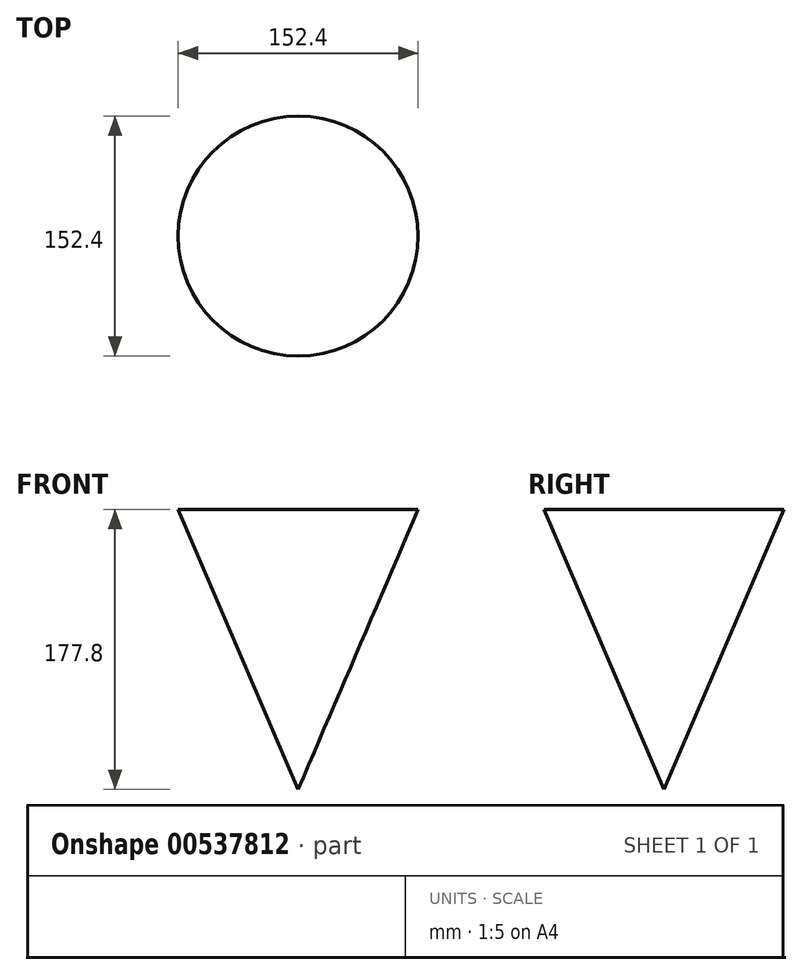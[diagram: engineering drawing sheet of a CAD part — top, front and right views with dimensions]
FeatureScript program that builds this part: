
annotation { "Feature Type Name" : "Feature", "Feature Type Description" : "" }
export const myFeature = defineFeature(function(context is Context, id is Id, definition is map)
    precondition{}
    {
        {
            var Q0;
            Q0=qCreatedBy(makeId("Front.planeOp"),FACE);
            var sketch = newSketch(context, id + "F0", { "sketchPlane" : qUnion([Q0])});
            skLineSegment(sketch, "E0", {"start": v(0, 88.9) * mm, "end": v(0, -88.9) * mm});
            skLineSegment(sketch, "E1", {"start": v(0, -88.9) * mm, "end": v(76.2, 88.9) * mm});
            skLineSegment(sketch, "E2", {"start": v(76.2, 88.9) * mm, "end": v(0, 88.9) * mm});
            skSolve(sketch);
        }
        {
            var Q0;
            Q0=makeQuery(id+"F0.imprint","IMPRINT",FACE,{"disambiguationData":[TD([[makeQuery(id+"F0.imprint","IMPRINT",EDGE,{"derivedFrom":sQuery(id+"F0.wireOp",EDGE,"E0")}),1.0]])]});
            var Q1;
            Q1=sQuery(id+"F0.wireOp",EDGE,"E0");
            revolve(context, id + "F1", {"entities" : qUnion([Q0]), "axis" : qUnion([Q1]), "revolveType" : RevolveType.FULL});
        }
    });
